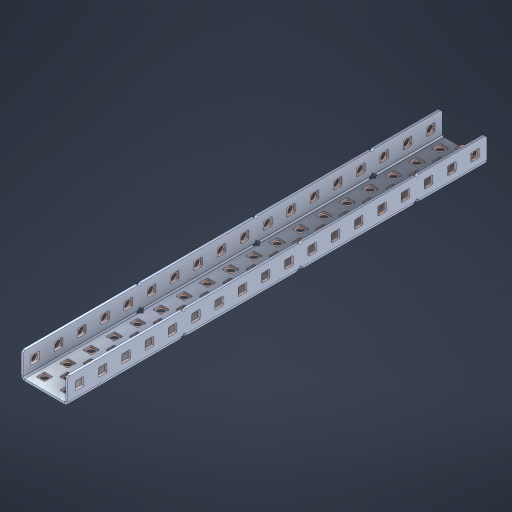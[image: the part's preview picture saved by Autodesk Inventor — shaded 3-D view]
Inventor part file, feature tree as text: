
AUTODESK INVENTOR PART (.ipt)
format: ipt  version: 2023 (Build 270158000, 158)  size: 1,301,504 bytes
history: native  units: in
note: dims shown in document units (in); Inventor stores cm internally (conversion verified against a paired STEP export)
features: other x97, extrude x88, sheet_metal_op x11, sketch x10, pattern_linear x2, mirror x1, chamfer x1
ambient origin geometry x8: Origin, YZ Plane, XZ Plane, XY Plane, X Axis, Y Axis, Z Axis, Center Point
bodies: Solid1 (feature_tree), Body (feature_tree)
feature tree (210):
  sheet_metal_op  "Flanges"
  other  "Flange Pattern Plane"
  other  "Flange Pattern Sketch"
  sheet_metal_op  "Flange Pattern"
  sheet_metal_op  "Body Pattern"
  pattern_linear  "Center Pattern"  Spacing1=0.0469in  [1 undecoded]
  other  "Arc Length"
  mirror  "Notch Mirror"
  pattern_linear  "Notch Pattern"  Spacing1=0.182in  [1 undecoded]
  chamfer  "End Chamfer"
  extrude  "Half Cut"  Depth=0.02in
  sketch  "Sketch1"  dims[d0=1.0in]
  other  "Plate1"
  sketch  "Sketch2"  dims[d1=9.0in]
  other  "Plate2"
  sheet_metal_op  "Bend1"
  sheet_metal_op  "Corner1"
  sketch  "Sketch3"  dims[d2=0.0469in]
  sketch  "Sketch7"  dims[d3=0.0469in]
  other  "Srf1"
  other  "Srf2"
  sketch  "Sketch8"  dims[d4=0.0234in]
  sketch  "Sketch9"  dims[d5=0.0938in]
  other  "Srf91"
  sheet_metal_op  "Body Pattern Sketch"
  other  "Srf92"
  sketch  "Sketch13"  dims[d6=0.0469in]
  sketch  "Sketch14"  dims[d7=0.5in d8=90.0deg d9=0.0312in]
  sketch  "Sketch15"  dims[d10=0.1875in]
  sketch  "Sketch16"  dims[d11=0.0469in d12=0.0469in d16=0.182in d17=0.02in d18=0.0469in d19=0.0in d20=0.25in d21=0.25in d38=7.0866in d40=0.5in d41=0.7874in d43=1.0in d46=0.172in d47=1.0in d48=0.0in d49=0.182in d50=0.02in d51=0.25in d52=0.25in d53=0.0469in d54=0.0in d55=0.172in d56=1.0in d57=0.0in d58=0.25in d60=7.0866in d62=0.5in d63=0.7874in d65=0.5in d85=0.1227in d86=0.1659in d88=0.04in d89=0.0469in d90=0.0in d91=0.04in d92=0.0491in d95=2.5in d96=0.04in d97=0.25in d98=45.0deg d99=0.25in d100=0.5in d101=0.0in d102=2.497in d106=0.182in d107=0.02in d108=0.5in d109=0.5in d110=0.0469in d111=0.0in d112=0.172in d113=0.5in d114=0.0in d117=0.5in d118=0.5in d119=0.5in]
  other  "Srf786"
  other  "Srf823"
  other  "Srf824"
  other  "Srf825"
  other  "Srf826"
  other  "Srf827"
  other  "Srf828"
  other  "Srf829"
  other  "Srf856"
  other  "Srf857"
  other  "Srf858"
  other  "Srf859"
  other  "Srf860"
  other  "Srf861"
  other  "Srf862"
  other  "Srf889"
  other  "Srf890"
  other  "Srf891"
  other  "Srf892"
  other  "Srf893"
  other  "Srf894"
  other  "Srf895"
  other  "Srf896"
  other  "Srf922"
  other  "Srf923"
  other  "Srf924"
  other  "Srf925"
  other  "Srf926"
  other  "Srf959"
  other  "Srf960"
  other  "Srf961"
  other  "Srf962"
  other  "Srf963"
  other  "Srf996"
  other  "Srf997"
  other  "Srf998"
  other  "Srf999"
  other  "Srf1000"
  other  "Srf1143"
  other  "Srf1144"
  other  "Srf1145"
  other  "Srf1146"
  other  "Srf1147"
  other  "Srf1148"
  other  "Srf1149"
  other  "Srf1150"
  other  "Srf1151"
  other  "Srf1152"
  other  "Srf1153"
  other  "Srf1154"
  other  "Srf1155"
  other  "Srf1156"
  other  "Srf1157"
  other  "Srf1158"
  other  "Srf1159"
  other  "Srf1160"
  other  "Srf1161"
  other  "Srf1162"
  other  "Srf1163"
  other  "Srf1164"
  other  "Srf1199"
  other  "Srf1200"
  other  "Srf1201"
  other  "Srf1202"
  other  "Srf1203"
  other  "Srf1204"
  other  "Srf1205"
  other  "Srf1206"
  other  "Srf1207"
  other  "Srf1208"
  other  "Srf1209"
  other  "Srf1210"
  other  "Srf1211"
  other  "Srf1212"
  other  "Srf1213"
  other  "Srf1214"
  other  "Srf1215"
  other  "Srf1216"
  other  "Srf1217"
  other  "Srf1218"
  other  "Srf1219"
  other  "Srf1220"
  other  "Srf1255"
  other  "Srf1256"
  other  "Srf1257"
  other  "Srf1258"
  sheet_metal_op  "Flange Stamp"
  sheet_metal_op  "Flange Circle"
  sheet_metal_op  "Body Stamp"
  sheet_metal_op  "Body Circle"
  other  "Center Stamp"
  other  "Center Circle"
  sheet_metal_op  "Notch"
  extrude  "ExtrusionSrf2"  Depth=0.0469in
  extrude  "ExtrusionSrf92"  TaperAngle=0.0deg  [1 undecoded]
  extrude  "ExtrusionSrf823"  Depth=0.5in
  extrude  "ExtrusionSrf824"  Depth=0.5in
  extrude  "ExtrusionSrf825"  Depth=0.5in
  extrude  "ExtrusionSrf826"  Depth=0.5in
  extrude  "ExtrusionSrf827"  Depth=1.0in TaperAngle=0.0deg
  extrude  "ExtrusionSrf828"  Depth=0.5in
  extrude  "ExtrusionSrf829"  Depth=0.02in
  extrude  "ExtrusionSrf856"  Depth=0.5in
  extrude  "ExtrusionSrf857"  Depth=0.5in
  extrude  "ExtrusionSrf858"  Depth=0.0469in
  extrude  "ExtrusionSrf859"  TaperAngle=0.0deg  [1 undecoded]
  extrude  "ExtrusionSrf860"  Depth=0.5in
  extrude  "ExtrusionSrf861"  Depth=1.0in TaperAngle=0.0deg
  extrude  "ExtrusionSrf862"  Depth=0.5in
  extrude  "ExtrusionSrf889"  Depth=0.5in
  extrude  "ExtrusionSrf890"  Depth=0.5in
  extrude  "ExtrusionSrf891"  Depth=0.5in
  extrude  "ExtrusionSrf892"  Depth=0.5in
  extrude  "ExtrusionSrf893"  Depth=0.5in
  extrude  "ExtrusionSrf894"  Depth=0.0469in
  extrude  "ExtrusionSrf895"  TaperAngle=0.0deg  [1 undecoded]
  extrude  "ExtrusionSrf896"  Depth=0.5in
  extrude  "ExtrusionSrf922"  Depth=0.5in
  extrude  "ExtrusionSrf923"  Depth=2.5in
  extrude  "ExtrusionSrf924"  Depth=0.5in TaperAngle=45.0deg
  extrude  "ExtrusionSrf925"  Depth=0.5in
  extrude  "ExtrusionSrf926"  Depth=0.5in TaperAngle=0.0deg
  extrude  "ExtrusionSrf959"  Depth=0.5in
  extrude  "ExtrusionSrf960"  Depth=0.5in
  extrude  "ExtrusionSrf961"  Depth=0.02in
  extrude  "ExtrusionSrf962"  Depth=0.5in
  extrude  "ExtrusionSrf963"  Depth=0.5in
  extrude  "ExtrusionSrf996"  Depth=0.0469in
  extrude  "ExtrusionSrf997"  TaperAngle=0.0deg  [1 undecoded]
  extrude  "ExtrusionSrf998"  Depth=0.5in
  extrude  "ExtrusionSrf999"  Depth=0.5in TaperAngle=0.0deg
  extrude  "ExtrusionSrf1000"  Depth=0.5in
  extrude  "ExtrusionSrf1143"  Depth=0.5in
  extrude  "ExtrusionSrf1144"  Depth=0.5in
  extrude  "ExtrusionSrf1145"  [1 undecoded]
  extrude  "ExtrusionSrf1146"  [1 undecoded]
  extrude  "ExtrusionSrf1147"  [1 undecoded]
  extrude  "ExtrusionSrf1148"  [1 undecoded]
  extrude  "ExtrusionSrf1149"  [1 undecoded]
  extrude  "ExtrusionSrf1150"  [1 undecoded]
  extrude  "ExtrusionSrf1151"  [1 undecoded]
  extrude  "ExtrusionSrf1152"  [1 undecoded]
  extrude  "ExtrusionSrf1153"  [1 undecoded]
  extrude  "ExtrusionSrf1154"  [1 undecoded]
  extrude  "ExtrusionSrf1155"  [1 undecoded]
  extrude  "ExtrusionSrf1156"  [1 undecoded]
  extrude  "ExtrusionSrf1157"  [1 undecoded]
  extrude  "ExtrusionSrf1158"  [1 undecoded]
  extrude  "ExtrusionSrf1159"  [1 undecoded]
  extrude  "ExtrusionSrf1160"  [1 undecoded]
  extrude  "ExtrusionSrf1161"  [1 undecoded]
  extrude  "ExtrusionSrf1162"  [1 undecoded]
  extrude  "ExtrusionSrf1163"  [1 undecoded]
  extrude  "ExtrusionSrf1164"  [1 undecoded]
  extrude  "ExtrusionSrf1199"  [1 undecoded]
  extrude  "ExtrusionSrf1200"  [1 undecoded]
  extrude  "ExtrusionSrf1201"  [1 undecoded]
  extrude  "ExtrusionSrf1202"  [1 undecoded]
  extrude  "ExtrusionSrf1203"  [1 undecoded]
  extrude  "ExtrusionSrf1204"  [1 undecoded]
  extrude  "ExtrusionSrf1205"  [1 undecoded]
  extrude  "ExtrusionSrf1206"  [1 undecoded]
  extrude  "ExtrusionSrf1207"  [1 undecoded]
  extrude  "ExtrusionSrf1208"  [1 undecoded]
  extrude  "ExtrusionSrf1209"  [1 undecoded]
  extrude  "ExtrusionSrf1210"  [1 undecoded]
  extrude  "ExtrusionSrf1211"  [1 undecoded]
  extrude  "ExtrusionSrf1212"  [1 undecoded]
  extrude  "ExtrusionSrf1213"  [1 undecoded]
  extrude  "ExtrusionSrf1214"  [1 undecoded]
  extrude  "ExtrusionSrf1215"  [1 undecoded]
  extrude  "ExtrusionSrf1216"  [1 undecoded]
  extrude  "ExtrusionSrf1217"  [1 undecoded]
  extrude  "ExtrusionSrf1218"  [1 undecoded]
  extrude  "ExtrusionSrf1219"  [1 undecoded]
  extrude  "ExtrusionSrf1220"  [1 undecoded]
  extrude  "ExtrusionSrf1255"  [1 undecoded]
  extrude  "ExtrusionSrf1256"  [1 undecoded]
  extrude  "ExtrusionSrf1257"  [1 undecoded]
  extrude  "ExtrusionSrf1258"  [1 undecoded]
note: 52 required parameter values undecoded (feature->parameter linkage not recoverable at this tier; creation-order binding heuristic only, values carry confidence <= 0.55)
